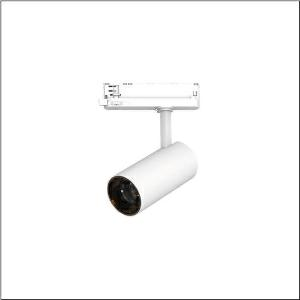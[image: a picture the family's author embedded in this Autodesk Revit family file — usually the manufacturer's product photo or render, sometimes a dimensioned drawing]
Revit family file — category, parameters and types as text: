
# Revit family: spot_31_slim_51sf127fa2b
name_source: partatom
category: Lighting Fixtures
units: mm (PartAtom-declared; Revit-internal decimal feet)

## family parameters
Cut with Voids When Loaded = No
Host = Face
Light Source = No
Part Type = Normal
Room Calculation Point = No
Round Connector Dimension = Use Diameter
Shared = No

## types (1)
- Spot 31 Slim (1 x LED, 2090 lm, 16.3 W, 2700K)
    Apparent Load = 16 VA
    CIE Flux Codes = 94 98 99 100 100
    Color Rendering = 90
    Color Temperature = 2700K
    Default Elevation = 1800 mm
    Description = Spot 31 Slim, directional spotlight, light control with reflector, of aluminium, LED rated luminous flux: 2.100lm, light colour: 927, control gear: ECG, with 3-phase adapter, mains connection: 220..240V, AC, 50/60Hz, housing, of aluminium, traffic white (RAL 9016), diameter: 70mm, adapter, of plastic, protection rating (complete): IP20, insulation class (complete): insulation class I (protective earthing), certification: CE, impact resistance: IK02, packaging unit: 1 piece
    Height = 210 mm
    Lamp = 1 x LED
    Lamp Light Flux = 2090 lm
    Lamp Power = 16.3 W
    Lamp count = 1
    Length = 70 mm
    Luminous efficacy = 128 lm/W
    Manufacturer = Siteco
    ModVariant = No
    Model = 51SF127FA2B
    Mounting Place = Ceiling
    Mounting Type = Pendant
    Number of Poles = 1
    OnlyDefault = Yes
    Power Factor = 1
    Product Name = Spot 31 Slim
    Product group = directional spotlight
    ProductGroupID = 905
    Protection Class = Protection class I
    Protection Degree = IP 20
    RLX_Detail_Level = 1
    RLX_Emergency_Light_Flux = 0 lm
    RLX_Emergency_Type = 0
    RLX_Emergency_Type_DB = No
    RlxData = <blob elided: 14169 chars, md5=6e41c0dd>
    Socket = socket
    Standby Power = 0 W
    System Light Flux = 2090 lm
    System Power = 16 W
    Type Comments = Product without accessories
    Type Image = l_1228468.jpg
    URL = http://relux.com
    VarID = ---
    Voltage = 0 V
    Weight = 0.00 kg
    Width = 0 mm  [stored 0 ft]

note: [stored X ft] marks values corroborated as IEEE doubles in the binary element streams (Revit-internal decimal feet)

## geometry (parser evidence)
native form markers: Sweep x11
no freeform markers — native parametric forms only
